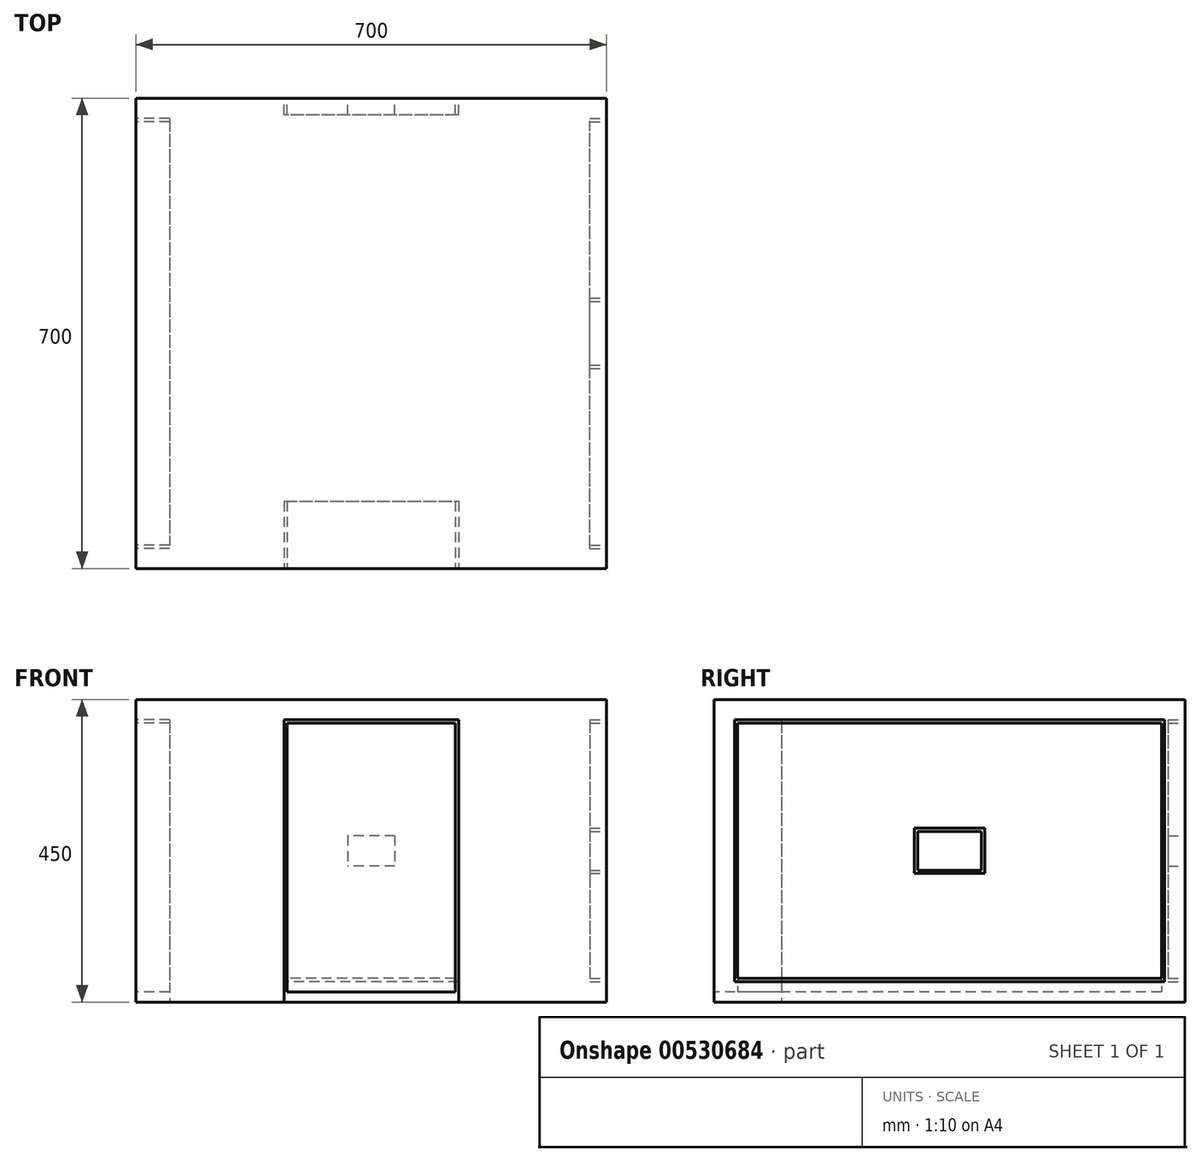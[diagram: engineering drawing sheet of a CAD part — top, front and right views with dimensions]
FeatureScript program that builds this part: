
annotation { "Feature Type Name" : "Feature", "Feature Type Description" : "" }
export const myFeature = defineFeature(function(context is Context, id is Id, definition is map)
    precondition{}
    {
        {
            var Q0;
            Q0=qCreatedBy(makeId("Top.planeOp"),FACE);
            var sketch = newSketch(context, id + "F0", { "sketchPlane" : qUnion([Q0])});
            skLineSegment(sketch, "E0.bottom", {"start": v(-350, 350) * mm, "end": v(350, 350) * mm});
            skLineSegment(sketch, "E0.top", {"start": v(-350, -350) * mm, "end": v(350, -350) * mm});
            skLineSegment(sketch, "E0.left", {"start": v(-350, 350) * mm, "end": v(-350, -350) * mm});
            skLineSegment(sketch, "E0.right", {"start": v(350, 350) * mm, "end": v(350, -350) * mm});
            skSolve(sketch);
        }
        {
            var Q0;
            Q0=makeQuery(id+"F0.imprint","IMPRINT",FACE,{"disambiguationData":[TD([[makeQuery(id+"F0.imprint","IMPRINT",EDGE,{"derivedFrom":sQuery(id+"F0.wireOp",EDGE,"E0.bottom")}),-1.0]])]});
            extrude(context, id + "F1", {"entities" : qUnion([Q0]), "depth" : 450 * mm, "offsetDistance" : 25 * mm});
        }
        {
            var Q0;
            Q0=makeQuery(id+"F1.opExtrude","SWEPT_FACE",FACE,{"disambiguationData":[OSD([sQuery(id+"F0.wireOp",EDGE,"E0.right")])]});
            var sketch = newSketch(context, id + "F2", { "sketchPlane" : qUnion([Q0])});
            skLineSegment(sketch, "E1.bottom", {"start": v(-320, 420) * mm, "end": v(320, 420) * mm});
            skLineSegment(sketch, "E1.top", {"start": v(-320, 30) * mm, "end": v(320, 30) * mm});
            skLineSegment(sketch, "E1.left", {"start": v(-320, 420) * mm, "end": v(-320, 30) * mm});
            skLineSegment(sketch, "E1.right", {"start": v(320, 420) * mm, "end": v(320, 30) * mm});
            skLineSegment(sketch, "E2.bottom", {"start": v(-315, 415) * mm, "end": v(315, 415) * mm});
            skLineSegment(sketch, "E2.top", {"start": v(-315, 35) * mm, "end": v(315, 35) * mm});
            skLineSegment(sketch, "E2.left", {"start": v(-315, 415) * mm, "end": v(-315, 35) * mm});
            skLineSegment(sketch, "E2.right", {"start": v(315, 415) * mm, "end": v(315, 35) * mm});
            skSolve(sketch);
        }
        {
            var Q0;
            Q0=makeQuery(id+"F2.imprint","IMPRINT",FACE,{"disambiguationData":[TD([[makeQuery(id+"F2.imprint","IMPRINT",EDGE,{"derivedFrom":sQuery(id+"F2.wireOp",EDGE,"E1.bottom")}),-1.0]])]});
            extrude(context, id + "F3", {"entities" : qUnion([Q0]), "operationType" : NewBodyOperationType.REMOVE, "oppositeDirection" : true, "depth" : 25 * mm, "offsetDistance" : 25 * mm});
        }
        {
            var Q0;
            Q0=makeQuery(id+"F1.opExtrude","SWEPT_FACE",FACE,{"disambiguationData":[OSD([sQuery(id+"F0.wireOp",EDGE,"E0.bottom")])]});
            var sketch = newSketch(context, id + "F4", { "sketchPlane" : qUnion([Q0])});
            skLineSegment(sketch, "E3.bottom", {"start": v(-320, 420) * mm, "end": v(-160, 420) * mm});
            skLineSegment(sketch, "E3.top", {"start": v(-320, 30) * mm, "end": v(-160, 30) * mm});
            skLineSegment(sketch, "E3.left", {"start": v(-320, 420) * mm, "end": v(-320, 30) * mm});
            skLineSegment(sketch, "E3.right", {"start": v(-160, 420) * mm, "end": v(-160, 30) * mm});
            skLineSegment(sketch, "E4.bottom", {"start": v(-315, 415) * mm, "end": v(-165, 415) * mm});
            skLineSegment(sketch, "E4.top", {"start": v(-315, 35) * mm, "end": v(-165, 35) * mm});
            skLineSegment(sketch, "E4.left", {"start": v(-315, 415) * mm, "end": v(-315, 35) * mm});
            skLineSegment(sketch, "E4.right", {"start": v(-165, 415) * mm, "end": v(-165, 35) * mm});
            skLineSegment(sketch, "E5.bottom", {"start": v(-130, 420) * mm, "end": v(130, 420) * mm});
            skLineSegment(sketch, "E5.top", {"start": v(-130, 30) * mm, "end": v(130, 30) * mm});
            skLineSegment(sketch, "E5.left", {"start": v(-130, 420) * mm, "end": v(-130, 30) * mm});
            skLineSegment(sketch, "E5.right", {"start": v(130, 420) * mm, "end": v(130, 30) * mm});
            skLineSegment(sketch, "E6.bottom", {"start": v(-125, 415) * mm, "end": v(125, 415) * mm});
            skLineSegment(sketch, "E6.top", {"start": v(-125, 35) * mm, "end": v(125, 35) * mm});
            skLineSegment(sketch, "E6.left", {"start": v(-125, 415) * mm, "end": v(-125, 35) * mm});
            skLineSegment(sketch, "E6.right", {"start": v(125, 415) * mm, "end": v(125, 35) * mm});
            skLineSegment(sketch, "E7.bottom", {"start": v(160, 420) * mm, "end": v(320, 420) * mm});
            skLineSegment(sketch, "E7.top", {"start": v(160, 30) * mm, "end": v(320, 30) * mm});
            skLineSegment(sketch, "E7.left", {"start": v(160, 420) * mm, "end": v(160, 30) * mm});
            skLineSegment(sketch, "E7.right", {"start": v(320, 420) * mm, "end": v(320, 30) * mm});
            skLineSegment(sketch, "E8.bottom", {"start": v(165, 35) * mm, "end": v(315, 35) * mm});
            skLineSegment(sketch, "E8.top", {"start": v(165, 415) * mm, "end": v(315, 415) * mm});
            skLineSegment(sketch, "E8.left", {"start": v(165, 35) * mm, "end": v(165, 415) * mm});
            skLineSegment(sketch, "E8.right", {"start": v(315, 35) * mm, "end": v(315, 415) * mm});
            skLineSegment(sketch, "E9.bottom", {"start": v(-35, 247.5) * mm, "end": v(35, 247.5) * mm});
            skLineSegment(sketch, "E9.top", {"start": v(-35, 202.5) * mm, "end": v(35, 202.5) * mm});
            skLineSegment(sketch, "E9.left", {"start": v(-35, 247.5) * mm, "end": v(-35, 202.5) * mm});
            skLineSegment(sketch, "E9.right", {"start": v(35, 247.5) * mm, "end": v(35, 202.5) * mm});
            skLineSegment(sketch, "E10.bottom", {"start": v(-225, 247.5) * mm, "end": v(-242, 247.5) * mm});
            skLineSegment(sketch, "E10.top", {"start": v(-225, 202.5) * mm, "end": v(-242, 202.5) * mm});
            skLineSegment(sketch, "E10.left", {"start": v(-225, 247.5) * mm, "end": v(-225, 202.5) * mm});
            skLineSegment(sketch, "E10.right", {"start": v(-242, 247.5) * mm, "end": v(-242, 202.5) * mm});
            skPoint(sketch, "E11.oppositeSnap0", {"position": v(0, 202.5) * mm});
            skLineSegment(sketch, "E11.bottom", {"start": v(225, 247.5) * mm, "end": v(242, 247.5) * mm});
            skLineSegment(sketch, "E11.top", {"start": v(225, 202.5) * mm, "end": v(242, 202.5) * mm});
            skLineSegment(sketch, "E11.left", {"start": v(225, 247.5) * mm, "end": v(225, 202.5) * mm});
            skLineSegment(sketch, "E11.right", {"start": v(242, 247.5) * mm, "end": v(242, 202.5) * mm});
            skSolve(sketch);
        }
        {
            var Q0;
            Q0=makeQuery(id+"F4.imprint","IMPRINT",FACE,{"disambiguationData":[TD([[makeQuery(id+"F4.imprint","IMPRINT",EDGE,{"derivedFrom":sQuery(id+"F4.wireOp",EDGE,"E5.bottom")}),-1.0]])]});
            extrude(context, id + "F5", {"entities" : qUnion([Q0]), "operationType" : NewBodyOperationType.REMOVE, "oppositeDirection" : true, "depth" : 25 * mm, "offsetDistance" : 25 * mm});
        }
        {
            var Q0;
            Q0=makeQuery(id+"F3.boolean.opBoolean","SPLIT",FACE,{"disambiguationData":[TD([makeQuery(id+"F3.opExtrude","SWEPT_FACE",FACE,{"disambiguationData":[OSD([sQuery(id+"F2.wireOp",EDGE,"E2.bottom")])]})])],"derivedFrom":makeQuery(id+"F1.opExtrude","SWEPT_FACE",FACE,{"disambiguationData":[OSD([sQuery(id+"F0.wireOp",EDGE,"E0.right")])]})});
            var sketch = newSketch(context, id + "F6", { "sketchPlane" : qUnion([Q0])});
            skLineSegment(sketch, "E12.bottom", {"start": v(-52.5, 258.75) * mm, "end": v(52.5, 258.75) * mm});
            skLineSegment(sketch, "E12.top", {"start": v(-52.5, 191.25) * mm, "end": v(52.5, 191.25) * mm});
            skLineSegment(sketch, "E12.left", {"start": v(-52.5, 258.75) * mm, "end": v(-52.5, 191.25) * mm});
            skLineSegment(sketch, "E12.right", {"start": v(52.5, 258.75) * mm, "end": v(52.5, 191.25) * mm});
            skLineSegment(sketch, "E13", {"start": v(-137.6, 225) * mm, "end": v(241.67, 225) * mm});
            skLineSegment(sketch, "E14.bottom", {"start": v(-47.5, 253.75) * mm, "end": v(47.5, 253.75) * mm});
            skLineSegment(sketch, "E14.top", {"start": v(-47.5, 196.25) * mm, "end": v(47.5, 196.25) * mm});
            skLineSegment(sketch, "E14.left", {"start": v(-47.5, 253.75) * mm, "end": v(-47.5, 196.25) * mm});
            skLineSegment(sketch, "E14.right", {"start": v(47.5, 253.75) * mm, "end": v(47.5, 196.25) * mm});
            skSolve(sketch);
        }
        {
            var Q0;
            Q0=makeQuery(id+"F6.imprint","IMPRINT",FACE,{"disambiguationData":[TD([[makeQuery(id+"F6.imprint","IMPRINT",EDGE,{"derivedFrom":sQuery(id+"F6.wireOp",EDGE,"E12.bottom")}),-1.0]])]});
            var Q1;
            {var subQ1=sQuery(id+"F6.wireOp",EDGE,"E12.top");Q1=makeQuery(id+"F6.imprint","IMPRINT",FACE,{"disambiguationData":[TD([[makeQuery(id+"F6.imprint","IMPRINT",EDGE,{"derivedFrom":subQ1}),1.0]])]});}
            extrude(context, id + "F7", {"entities" : qUnion([Q0, Q1]), "operationType" : NewBodyOperationType.REMOVE, "oppositeDirection" : true, "depth" : 25 * mm, "offsetDistance" : 25 * mm});
        }
        {
            var Q0;
            Q0=makeQuery(id+"F4.imprint","IMPRINT",FACE,{"disambiguationData":[TD([[makeQuery(id+"F4.imprint","IMPRINT",EDGE,{"derivedFrom":sQuery(id+"F4.wireOp",EDGE,"E9.bottom")}),-1.0]])]});
            extrude(context, id + "F8", {"entities" : qUnion([Q0]), "operationType" : NewBodyOperationType.REMOVE, "oppositeDirection" : true, "depth" : 25 * mm, "offsetDistance" : 25 * mm});
        }
        {
            var Q0;
            Q0=makeQuery(id+"F1.opExtrude","SWEPT_FACE",FACE,{"disambiguationData":[OSD([sQuery(id+"F0.wireOp",EDGE,"E0.left")])]});
            var sketch = newSketch(context, id + "F9", { "sketchPlane" : qUnion([Q0])});
            skLineSegment(sketch, "E15.bottom", {"start": v(-320, 420) * mm, "end": v(320, 420) * mm});
            skLineSegment(sketch, "E15.top", {"start": v(-320, -102.87) * mm, "end": v(320, -102.87) * mm});
            skLineSegment(sketch, "E15.left", {"start": v(-320, 420) * mm, "end": v(-320, -102.87) * mm});
            skLineSegment(sketch, "E15.right", {"start": v(320, 420) * mm, "end": v(320, -102.87) * mm});
            skLineSegment(sketch, "E16.bottom", {"start": v(-315, 415) * mm, "end": v(315, 415) * mm});
            skLineSegment(sketch, "E16.top", {"start": v(-315, 15) * mm, "end": v(315, 15) * mm});
            skLineSegment(sketch, "E16.left", {"start": v(-315, 415) * mm, "end": v(-315, 15) * mm});
            skLineSegment(sketch, "E16.right", {"start": v(315, 415) * mm, "end": v(315, 15) * mm});
            skSolve(sketch);
        }
        {
            var Q0;
            {var subQ1=sQuery(id+"F9.wireOp",EDGE,"E15.bottom");Q0=makeQuery(id+"F9.imprint","IMPRINT",FACE,{"disambiguationData":[TD([[makeQuery(id+"F9.imprint","IMPRINT",EDGE,{"derivedFrom":subQ1}),-1.0]])]});}
            extrude(context, id + "F10", {"entities" : qUnion([Q0]), "operationType" : NewBodyOperationType.REMOVE, "oppositeDirection" : true, "depth" : 50 * mm, "offsetDistance" : 25 * mm});
        }
        {
            var Q0;
            Q0=makeQuery(id+"F1.opExtrude","SWEPT_FACE",FACE,{"disambiguationData":[OSD([sQuery(id+"F0.wireOp",EDGE,"E0.top")])]});
            var sketch = newSketch(context, id + "F11", { "sketchPlane" : qUnion([Q0])});
            skSolve(sketch);
        }
        {
            var Q0;
            {var subQ0=sQuery(id+"F0.wireOp",EDGE,"E0.top");Q0=makeQuery(id+"F11.imprint","IMPRINT",FACE,{"disambiguationData":[TD([[makeQuery(id+"F11.imprint","IMPRINT",EDGE,{"derivedFrom":makeQuery(id+"F1.opExtrude","CAP_EDGE",EDGE,{"disambiguationData":[OSD([subQ0])],"isStart":true})}),1.0]])]});}
            var sketch = newSketch(context, id + "F12", { "sketchPlane" : qUnion([Q0])});
            skLineSegment(sketch, "E17.bottom", {"start": v(-130, 420) * mm, "end": v(130, 420) * mm});
            skLineSegment(sketch, "E17.top", {"start": v(-130, -48.85) * mm, "end": v(130, -48.85) * mm});
            skLineSegment(sketch, "E17.left", {"start": v(-130, 420) * mm, "end": v(-130, -48.85) * mm});
            skLineSegment(sketch, "E17.right", {"start": v(130, 420) * mm, "end": v(130, -48.85) * mm});
            skLineSegment(sketch, "E18.bottom", {"start": v(-125, 415) * mm, "end": v(125, 415) * mm});
            skLineSegment(sketch, "E18.top", {"start": v(-125, 15) * mm, "end": v(125, 15) * mm});
            skLineSegment(sketch, "E18.left", {"start": v(-125, 415) * mm, "end": v(-125, 15) * mm});
            skLineSegment(sketch, "E18.right", {"start": v(125, 415) * mm, "end": v(125, 15) * mm});
            skSolve(sketch);
        }
        {
            var Q0;
            {var subQ1=sQuery(id+"F12.wireOp",EDGE,"E17.bottom");Q0=makeQuery(id+"F12.imprint","IMPRINT",FACE,{"disambiguationData":[TD([[makeQuery(id+"F12.imprint","IMPRINT",EDGE,{"derivedFrom":subQ1}),-1.0]])]});}
            extrude(context, id + "F13", {"entities" : qUnion([Q0]), "operationType" : NewBodyOperationType.REMOVE, "oppositeDirection" : true, "depth" : 100 * mm, "offsetDistance" : 25 * mm});
        }
    });
